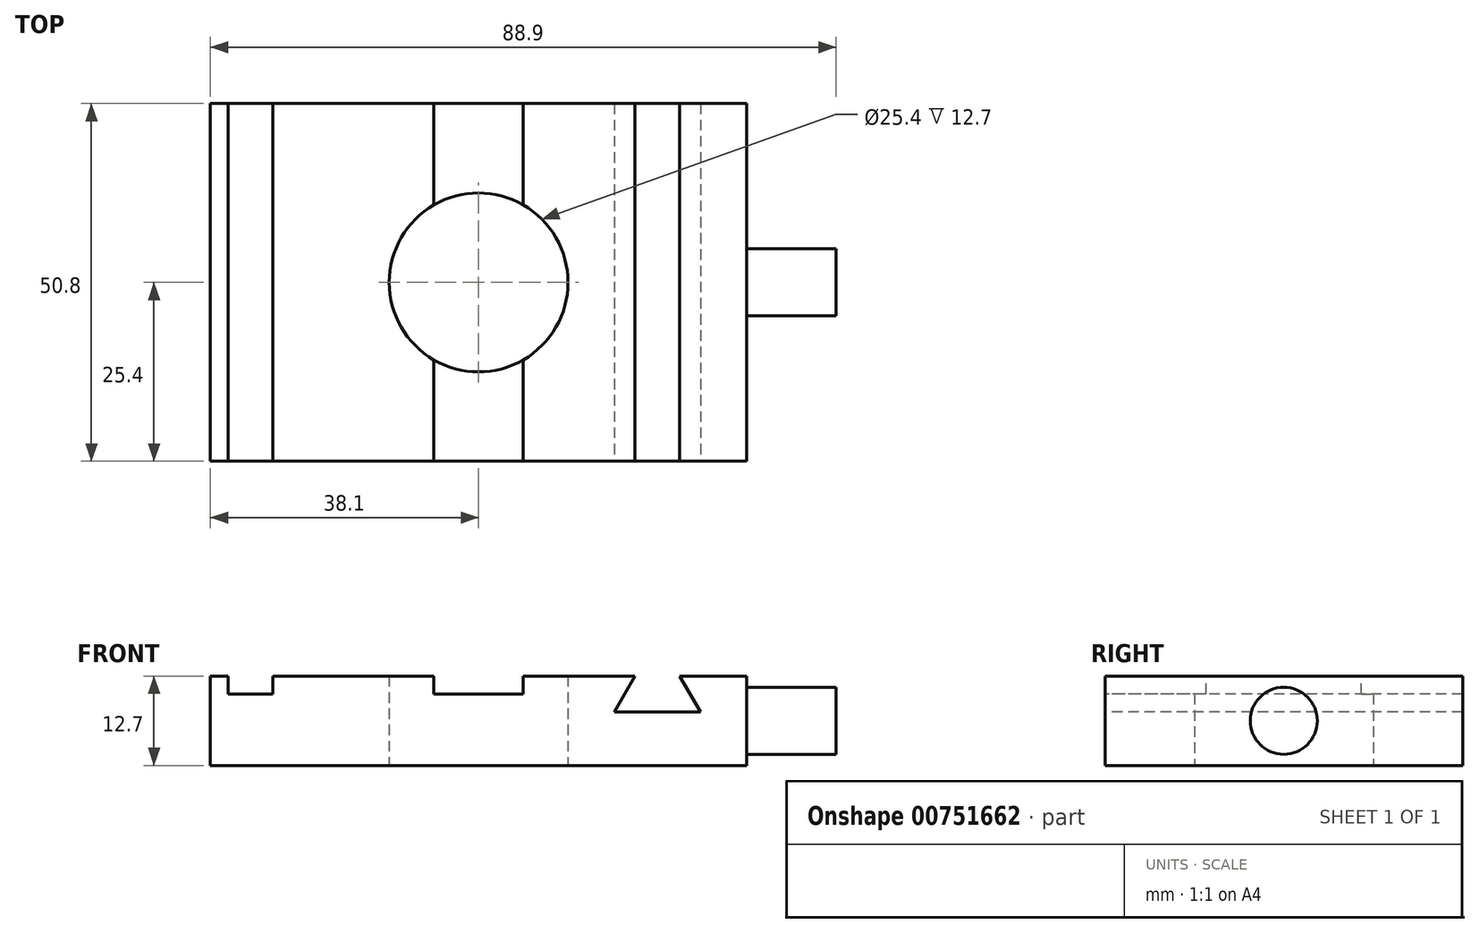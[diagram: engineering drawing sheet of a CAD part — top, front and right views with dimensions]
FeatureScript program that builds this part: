
annotation { "Feature Type Name" : "Feature", "Feature Type Description" : "" }
export const myFeature = defineFeature(function(context is Context, id is Id, definition is map)
    precondition{}
    {
        {
            var Q0;
            Q0=qCreatedBy(makeId("Top.planeOp"),FACE);
            var sketch = newSketch(context, id + "F0", { "sketchPlane" : qUnion([Q0])});
            skLineSegment(sketch, "E0.bottom", {"start": v(-38.1, 25.4) * mm, "end": v(38.1, 25.4) * mm});
            skLineSegment(sketch, "E0.top", {"start": v(-38.1, -25.4) * mm, "end": v(38.1, -25.4) * mm});
            skLineSegment(sketch, "E0.left", {"start": v(-38.1, 25.4) * mm, "end": v(-38.1, -25.4) * mm});
            skLineSegment(sketch, "E0.right", {"start": v(38.1, 25.4) * mm, "end": v(38.1, -25.4) * mm});
            skPoint(sketch, "E0.middle", {"position": v(0, 0) * mm});
            skCircle(sketch, "E1", {"center": v(0, 0) * mm, "radius": 12.7 * mm});
            skSolve(sketch);
        }
        {
            var Q0;
            Q0=makeQuery(id+"F0.imprint","IMPRINT",FACE,{"disambiguationData":[TD([[makeQuery(id+"F0.imprint","IMPRINT",EDGE,{"derivedFrom":sQuery(id+"F0.wireOp",EDGE,"E0.bottom")}),-1.0]])]});
            extrude(context, id + "F1", {"entities" : qUnion([Q0]), "depth" : 12.7 * mm, "offsetDistance" : 25.4 * mm});
        }
        {
            var Q0;
            Q0=makeQuery(id+"F1.opExtrude","CAP_FACE",FACE,{"disambiguationData":[OSD([sQuery(id+"F0.wireOp",EDGE,"E0.bottom"),sQuery(id+"F0.wireOp",EDGE,"E0.top"),sQuery(id+"F0.wireOp",EDGE,"E0.left"),sQuery(id+"F0.wireOp",EDGE,"E0.right"),sQuery(id+"F0.wireOp",EDGE,"E1")])],"isStart":false});
            var sketch = newSketch(context, id + "F2", { "sketchPlane" : qUnion([Q0])});
            skLineSegment(sketch, "E2.bottom", {"start": v(-35.56, 25.4) * mm, "end": v(-29.21, 25.4) * mm});
            skLineSegment(sketch, "E2.top", {"start": v(-35.56, -25.4) * mm, "end": v(-29.21, -25.4) * mm});
            skLineSegment(sketch, "E2.left", {"start": v(-35.56, 25.4) * mm, "end": v(-35.56, -25.4) * mm});
            skLineSegment(sketch, "E2.right", {"start": v(-29.21, 25.4) * mm, "end": v(-29.21, -25.4) * mm});
            skLineSegment(sketch, "E3", {"start": v(-6.35, 25.4) * mm, "end": v(-6.35, -25.4) * mm});
            skLineSegment(sketch, "E4", {"start": v(-6.35, -25.4) * mm, "end": v(6.35, -25.4) * mm});
            skLineSegment(sketch, "E5", {"start": v(6.35, -25.4) * mm, "end": v(6.35, 25.4) * mm});
            skLineSegment(sketch, "E6", {"start": v(6.35, 25.4) * mm, "end": v(-6.35, 25.4) * mm});
            skLineSegment(sketch, "E7", {"start": v(0, 25.4) * mm, "end": v(0, -25.4) * mm, "construction": true});
            skSolve(sketch);
        }
        {
            var Q0;
            Q0=makeQuery(id+"F2.imprint","IMPRINT",FACE,{"disambiguationData":[TD([[makeQuery(id+"F2.imprint","IMPRINT",EDGE,{"derivedFrom":sQuery(id+"F2.wireOp",EDGE,"E2.bottom")}),-1.0]])]});
            var Q1;
            {var subQ0=sQuery(id+"F2.wireOp",EDGE,"E6");Q1=makeQuery(id+"F2.imprint","IMPRINT",FACE,{"disambiguationData":[TD([[makeQuery(id+"F2.imprint","IMPRINT",EDGE,{"derivedFrom":subQ0}),-1.0]])]});}
            var Q2;
            {var subQ0=sQuery(id+"F2.wireOp",EDGE,"E4");Q2=makeQuery(id+"F2.imprint","IMPRINT",FACE,{"disambiguationData":[TD([[makeQuery(id+"F2.imprint","IMPRINT",EDGE,{"derivedFrom":subQ0}),1.0]])]});}
            extrude(context, id + "F3", {"entities" : qUnion([Q0, Q1, Q2]), "operationType" : NewBodyOperationType.REMOVE, "oppositeDirection" : true, "depth" : 2.54 * mm, "offsetDistance" : 25.4 * mm});
        }
        {
            var Q0;
            Q0=makeQuery(id+"F1.opExtrude","SWEPT_FACE",FACE,{"disambiguationData":[OSD([sQuery(id+"F0.wireOp",EDGE,"E0.top")])]});
            var sketch = newSketch(context, id + "F4", { "sketchPlane" : qUnion([Q0])});
            skLineSegment(sketch, "E8", {"start": v(22.23, 12.7) * mm, "end": v(19.3, 7.62) * mm});
            skLineSegment(sketch, "E9", {"start": v(19.3, 7.62) * mm, "end": v(31.5, 7.62) * mm});
            skLineSegment(sketch, "E10", {"start": v(31.5, 7.62) * mm, "end": v(28.58, 12.7) * mm});
            skLineSegment(sketch, "E11", {"start": v(28.58, 12.7) * mm, "end": v(22.23, 12.7) * mm});
            skLineSegment(sketch, "E12", {"start": v(25.4, 12.7) * mm, "end": v(25.4, 7.62) * mm, "construction": true});
            skSolve(sketch);
        }
        {
            var Q0;
            Q0=makeQuery(id+"F4.imprint","IMPRINT",FACE,{"disambiguationData":[TD([[makeQuery(id+"F4.imprint","IMPRINT",EDGE,{"derivedFrom":sQuery(id+"F4.wireOp",EDGE,"E8")}),1.0]])]});
            extrude(context, id + "F5", {"entities" : qUnion([Q0]), "operationType" : NewBodyOperationType.REMOVE, "oppositeDirection" : true, "depth" : 65.28 * mm, "offsetDistance" : 25.4 * mm});
        }
        {
            var Q0;
            Q0=makeQuery(id+"F1.opExtrude","SWEPT_FACE",FACE,{"disambiguationData":[OSD([sQuery(id+"F0.wireOp",EDGE,"E0.right")])]});
            var sketch = newSketch(context, id + "F6", { "sketchPlane" : qUnion([Q0])});
            skCircle(sketch, "E13", {"center": v(0, 6.35) * mm, "radius": 4.76 * mm});
            skPoint(sketch, "E13.centerSnap0", {"position": v(-25.4, 6.35) * mm});
            skSolve(sketch);
        }
        {
            var Q0;
            Q0 = qSketchRegion(id + "F6", true);
            extrude(context, id + "F7", {"entities" : qUnion([Q0]), "operationType" : NewBodyOperationType.ADD, "depth" : 12.7 * mm, "offsetDistance" : 25.4 * mm});
        }
    });
